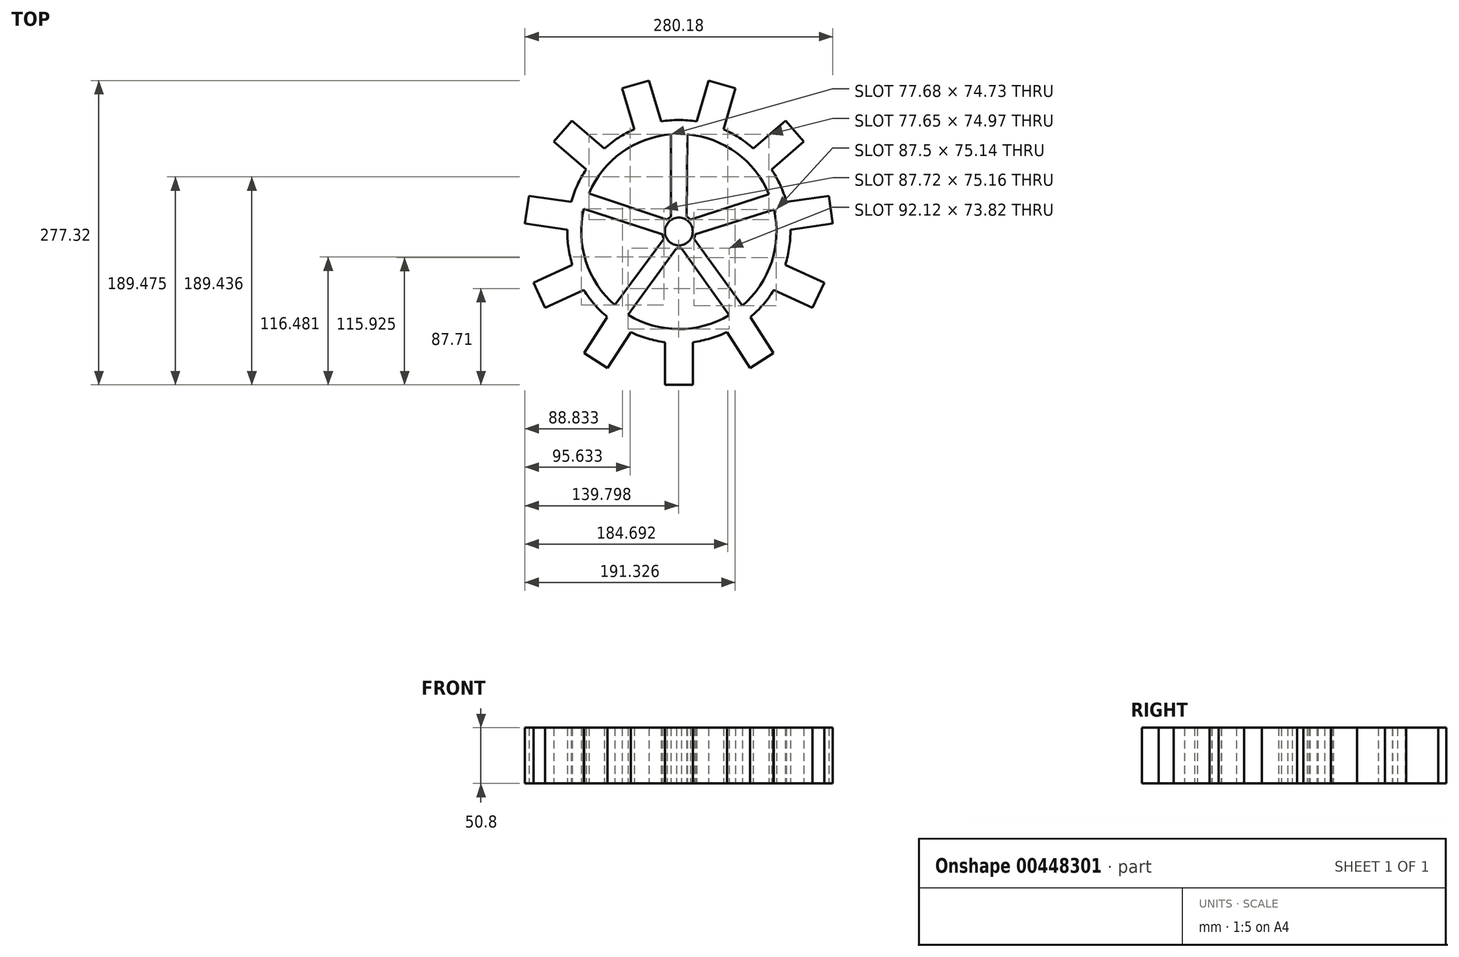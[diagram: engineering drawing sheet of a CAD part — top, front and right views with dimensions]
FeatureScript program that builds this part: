
annotation { "Feature Type Name" : "Feature", "Feature Type Description" : "" }
export const myFeature = defineFeature(function(context is Context, id is Id, definition is map)
    precondition{}
    {
        {
            var Q0;
            Q0=qCreatedBy(makeId("Top.planeOp"),FACE);
            var sketch = newSketch(context, id + "F0", { "sketchPlane" : qUnion([Q0])});
            skCircle(sketch, "E0", {"center": v(0, 0) * mm, "radius": 101.6 * mm});
            skLineSegment(sketch, "E1", {"start": v(-12.7, -100.8) * mm, "end": v(-12.7, -139.7) * mm});
            skLineSegment(sketch, "E2", {"start": v(-12.7, -139.7) * mm, "end": v(12.7, -139.7) * mm});
            skLineSegment(sketch, "E3", {"start": v(12.7, -139.7) * mm, "end": v(12.7, -100.8) * mm});
            skLineSegment(sketch, "E4.1.0", {"start": v(43.81, -91.67) * mm, "end": v(64.84, -124.39) * mm});
            skLineSegment(sketch, "E4.1.1", {"start": v(86.21, -110.66) * mm, "end": v(65.18, -77.93) * mm});
            skLineSegment(sketch, "E4.1.2", {"start": v(64.84, -124.39) * mm, "end": v(86.21, -110.66) * mm});
            skLineSegment(sketch, "E4.2.0", {"start": v(86.42, -53.43) * mm, "end": v(121.8, -69.59) * mm});
            skLineSegment(sketch, "E4.2.1", {"start": v(132.35, -46.48) * mm, "end": v(96.97, -30.32) * mm});
            skLineSegment(sketch, "E4.2.2", {"start": v(121.8, -69.59) * mm, "end": v(132.35, -46.48) * mm});
            skLineSegment(sketch, "E4.3.0", {"start": v(101.58, 1.78) * mm, "end": v(140.09, 7.31) * mm});
            skLineSegment(sketch, "E4.3.1", {"start": v(136.47, 32.45) * mm, "end": v(97.97, 26.92) * mm});
            skLineSegment(sketch, "E4.3.2", {"start": v(140.09, 7.31) * mm, "end": v(136.47, 32.45) * mm});
            skLineSegment(sketch, "E4.4.0", {"start": v(84.5, 56.41) * mm, "end": v(113.9, 81.89) * mm});
            skLineSegment(sketch, "E4.4.1", {"start": v(97.26, 101.08) * mm, "end": v(67.87, 75.61) * mm});
            skLineSegment(sketch, "E4.4.2", {"start": v(113.9, 81.89) * mm, "end": v(97.26, 101.08) * mm});
            skLineSegment(sketch, "E4.5.0", {"start": v(40.59, 93.14) * mm, "end": v(51.54, 130.46) * mm});
            skLineSegment(sketch, "E4.5.1", {"start": v(27.17, 137.62) * mm, "end": v(16.21, 100.3) * mm});
            skLineSegment(sketch, "E4.5.2", {"start": v(51.54, 130.46) * mm, "end": v(27.17, 137.62) * mm});
            skLineSegment(sketch, "E4.6.0", {"start": v(-16.21, 100.3) * mm, "end": v(-27.17, 137.62) * mm});
            skLineSegment(sketch, "E4.6.1", {"start": v(-51.54, 130.46) * mm, "end": v(-40.59, 93.14) * mm});
            skLineSegment(sketch, "E4.6.2", {"start": v(-27.17, 137.62) * mm, "end": v(-51.54, 130.46) * mm});
            skLineSegment(sketch, "E4.7.0", {"start": v(-67.87, 75.61) * mm, "end": v(-97.26, 101.08) * mm});
            skLineSegment(sketch, "E4.7.1", {"start": v(-113.9, 81.89) * mm, "end": v(-84.5, 56.41) * mm});
            skLineSegment(sketch, "E4.7.2", {"start": v(-97.26, 101.08) * mm, "end": v(-113.9, 81.89) * mm});
            skLineSegment(sketch, "E4.8.0", {"start": v(-97.97, 26.92) * mm, "end": v(-136.47, 32.45) * mm});
            skLineSegment(sketch, "E4.8.1", {"start": v(-140.09, 7.31) * mm, "end": v(-101.58, 1.78) * mm});
            skLineSegment(sketch, "E4.8.2", {"start": v(-136.47, 32.45) * mm, "end": v(-140.09, 7.31) * mm});
            skLineSegment(sketch, "E4.9.0", {"start": v(-96.97, -30.32) * mm, "end": v(-132.35, -46.48) * mm});
            skLineSegment(sketch, "E4.9.1", {"start": v(-121.8, -69.59) * mm, "end": v(-86.42, -53.43) * mm});
            skLineSegment(sketch, "E4.9.2", {"start": v(-132.35, -46.48) * mm, "end": v(-121.8, -69.59) * mm});
            skLineSegment(sketch, "E4.10.0", {"start": v(-65.18, -77.93) * mm, "end": v(-86.21, -110.66) * mm});
            skLineSegment(sketch, "E4.10.1", {"start": v(-64.84, -124.39) * mm, "end": v(-43.81, -91.67) * mm});
            skLineSegment(sketch, "E4.10.2", {"start": v(-86.21, -110.66) * mm, "end": v(-64.84, -124.39) * mm});
            skCircle(sketch, "E5", {"center": v(0, 0) * mm, "radius": 12.7 * mm});
            skLineSegment(sketch, "E6", {"start": v(-7.1, 101.35) * mm, "end": v(-7.1, 10.54) * mm});
            skLineSegment(sketch, "E7", {"start": v(7.88, 101.3) * mm, "end": v(7.1, 10.54) * mm});
            skLineSegment(sketch, "E8.1.0", {"start": v(-98.58, 24.58) * mm, "end": v(-12.21, -3.49) * mm});
            skLineSegment(sketch, "E8.1.1", {"start": v(-93.9, 38.8) * mm, "end": v(-7.83, 10) * mm});
            skLineSegment(sketch, "E8.2.0", {"start": v(-53.84, -86.16) * mm, "end": v(-0.46, -12.7) * mm});
            skLineSegment(sketch, "E8.2.1", {"start": v(-65.92, -77.32) * mm, "end": v(-11.93, -4.36) * mm});
            skLineSegment(sketch, "E8.3.0", {"start": v(65.3, -77.83) * mm, "end": v(11.93, -4.36) * mm});
            skLineSegment(sketch, "E8.3.1", {"start": v(53.16, -86.58) * mm, "end": v(0.46, -12.7) * mm});
            skLineSegment(sketch, "E8.4.0", {"start": v(94.2, 38.06) * mm, "end": v(7.83, 10) * mm});
            skLineSegment(sketch, "E8.4.1", {"start": v(98.77, 23.8) * mm, "end": v(12.21, -3.49) * mm});
            skCircle(sketch, "E9", {"center": v(0, 0) * mm, "radius": 88.9 * mm});
            skCircle(sketch, "E10", {"center": v(0, 0) * mm, "radius": 15.24 * mm});
            skSolve(sketch);
        }
        {
            var Q0;
            Q0 = qSketchRegion(id + "F0", true);
            var Q1;
            {var subQ0=sQuery(id+"F0.wireOp",EDGE,"E8.1.0");var subQ1=sQuery(id+"F0.wireOp",EDGE,"E5");var subQ2=makeQuery(id+"F0.imprint","INTERSECT",VERTEX,{"derivedFrom":[subQ1,subQ0]});Q1=makeQuery(id+"F0.imprint","IMPRINT",FACE,{"disambiguationData":[TD([[makeQuery(id+"F0.imprint","IMPRINT",EDGE,{"disambiguationData":[TD([[subQ2,1.0]])],"derivedFrom":subQ1}),-1.0]])]});}
            var Q2;
            {var subQ0=sQuery(id+"F0.wireOp",EDGE,"E6");var subQ1=sQuery(id+"F0.wireOp",EDGE,"E5");var subQ2=makeQuery(id+"F0.imprint","INTERSECT",VERTEX,{"derivedFrom":[subQ1,subQ0]});Q2=makeQuery(id+"F0.imprint","IMPRINT",FACE,{"disambiguationData":[TD([[makeQuery(id+"F0.imprint","IMPRINT",EDGE,{"disambiguationData":[TD([[subQ2,1.0]])],"derivedFrom":subQ1}),-1.0]])]});}
            var Q3;
            {var subQ0=sQuery(id+"F0.wireOp",EDGE,"E8.3.0");var subQ1=sQuery(id+"F0.wireOp",EDGE,"E5");var subQ2=makeQuery(id+"F0.imprint","INTERSECT",VERTEX,{"derivedFrom":[subQ1,subQ0]});Q3=makeQuery(id+"F0.imprint","IMPRINT",FACE,{"disambiguationData":[TD([[makeQuery(id+"F0.imprint","IMPRINT",EDGE,{"disambiguationData":[TD([[subQ2,1.0]])],"derivedFrom":subQ1}),-1.0]])]});}
            var Q4;
            {var subQ0=sQuery(id+"F0.wireOp",EDGE,"E8.2.0");var subQ1=sQuery(id+"F0.wireOp",EDGE,"E5");var subQ2=makeQuery(id+"F0.imprint","INTERSECT",VERTEX,{"derivedFrom":[subQ1,subQ0]});Q4=makeQuery(id+"F0.imprint","IMPRINT",FACE,{"disambiguationData":[TD([[makeQuery(id+"F0.imprint","IMPRINT",EDGE,{"disambiguationData":[TD([[subQ2,1.0]])],"derivedFrom":subQ1}),-1.0]])]});}
            var Q5;
            {var subQ0=sQuery(id+"F0.wireOp",EDGE,"E8.4.0");var subQ1=sQuery(id+"F0.wireOp",EDGE,"E5");var subQ2=makeQuery(id+"F0.imprint","INTERSECT",VERTEX,{"derivedFrom":[subQ1,subQ0]});Q5=makeQuery(id+"F0.imprint","IMPRINT",FACE,{"disambiguationData":[TD([[makeQuery(id+"F0.imprint","IMPRINT",EDGE,{"disambiguationData":[TD([[subQ2,1.0]])],"derivedFrom":subQ1}),-1.0]])]});}
            var Q6;
            {var subQ0=sQuery(id+"F0.wireOp",EDGE,"E9");var subQ1=sQuery(id+"F0.wireOp",EDGE,"E8.2.0");var subQ2=makeQuery(id+"F0.imprint","INTERSECT",VERTEX,{"derivedFrom":[subQ1,subQ0]});Q6=makeQuery(id+"F0.imprint","IMPRINT",FACE,{"disambiguationData":[TD([[makeQuery(id+"F0.imprint","IMPRINT",EDGE,{"disambiguationData":[TD([[subQ2,-1.0]])],"derivedFrom":subQ1}),1.0]])]});}
            var Q7;
            {var subQ0=sQuery(id+"F0.wireOp",EDGE,"E9");var subQ1=sQuery(id+"F0.wireOp",EDGE,"E8.3.0");var subQ2=makeQuery(id+"F0.imprint","INTERSECT",VERTEX,{"derivedFrom":[subQ1,subQ0]});Q7=makeQuery(id+"F0.imprint","IMPRINT",FACE,{"disambiguationData":[TD([[makeQuery(id+"F0.imprint","IMPRINT",EDGE,{"disambiguationData":[TD([[subQ2,-1.0]])],"derivedFrom":subQ1}),1.0]])]});}
            var Q8;
            {var subQ0=sQuery(id+"F0.wireOp",EDGE,"E9");var subQ1=sQuery(id+"F0.wireOp",EDGE,"E8.1.0");var subQ2=makeQuery(id+"F0.imprint","INTERSECT",VERTEX,{"derivedFrom":[subQ1,subQ0]});Q8=makeQuery(id+"F0.imprint","IMPRINT",FACE,{"disambiguationData":[TD([[makeQuery(id+"F0.imprint","IMPRINT",EDGE,{"disambiguationData":[TD([[subQ2,-1.0]])],"derivedFrom":subQ1}),1.0]])]});}
            var Q9;
            {var subQ0=sQuery(id+"F0.wireOp",EDGE,"E8.1.0");var subQ1=sQuery(id+"F0.wireOp",EDGE,"E5");var subQ2=makeQuery(id+"F0.imprint","INTERSECT",VERTEX,{"derivedFrom":[subQ1,subQ0]});Q9=makeQuery(id+"F0.imprint","IMPRINT",FACE,{"disambiguationData":[TD([[makeQuery(id+"F0.imprint","IMPRINT",EDGE,{"disambiguationData":[TD([[subQ2,-1.0]])],"derivedFrom":subQ1}),-1.0]])]});}
            var Q10;
            {var subQ0=sQuery(id+"F0.wireOp",EDGE,"E6");var subQ1=sQuery(id+"F0.wireOp",EDGE,"E5");var subQ2=makeQuery(id+"F0.imprint","INTERSECT",VERTEX,{"derivedFrom":[subQ1,subQ0]});Q10=makeQuery(id+"F0.imprint","IMPRINT",FACE,{"disambiguationData":[TD([[makeQuery(id+"F0.imprint","IMPRINT",EDGE,{"disambiguationData":[TD([[subQ2,-1.0]])],"derivedFrom":subQ1}),-1.0]])]});}
            var Q11;
            {var subQ0=sQuery(id+"F0.wireOp",EDGE,"E7");var subQ1=sQuery(id+"F0.wireOp",EDGE,"E5");var subQ2=makeQuery(id+"F0.imprint","INTERSECT",VERTEX,{"derivedFrom":[subQ1,subQ0]});Q11=makeQuery(id+"F0.imprint","IMPRINT",FACE,{"disambiguationData":[TD([[makeQuery(id+"F0.imprint","IMPRINT",EDGE,{"disambiguationData":[TD([[subQ2,1.0]])],"derivedFrom":subQ1}),-1.0]])]});}
            var Q12;
            {var subQ0=sQuery(id+"F0.wireOp",EDGE,"E9");var subQ1=sQuery(id+"F0.wireOp",EDGE,"E8.4.0");var subQ2=makeQuery(id+"F0.imprint","INTERSECT",VERTEX,{"derivedFrom":[subQ1,subQ0]});Q12=makeQuery(id+"F0.imprint","IMPRINT",FACE,{"disambiguationData":[TD([[makeQuery(id+"F0.imprint","IMPRINT",EDGE,{"disambiguationData":[TD([[subQ2,-1.0]])],"derivedFrom":subQ1}),1.0]])]});}
            var Q13;
            {var subQ0=sQuery(id+"F0.wireOp",EDGE,"E9");var subQ1=sQuery(id+"F0.wireOp",EDGE,"E6");var subQ2=makeQuery(id+"F0.imprint","INTERSECT",VERTEX,{"derivedFrom":[subQ1,subQ0]});Q13=makeQuery(id+"F0.imprint","IMPRINT",FACE,{"disambiguationData":[TD([[makeQuery(id+"F0.imprint","IMPRINT",EDGE,{"disambiguationData":[TD([[subQ2,-1.0]])],"derivedFrom":subQ1}),1.0]])]});}
            var Q14;
            {var subQ0=sQuery(id+"F0.wireOp",EDGE,"E8.2.0");var subQ1=sQuery(id+"F0.wireOp",EDGE,"E5");var subQ2=makeQuery(id+"F0.imprint","INTERSECT",VERTEX,{"derivedFrom":[subQ1,subQ0]});Q14=makeQuery(id+"F0.imprint","IMPRINT",FACE,{"disambiguationData":[TD([[makeQuery(id+"F0.imprint","IMPRINT",EDGE,{"disambiguationData":[TD([[subQ2,-1.0]])],"derivedFrom":subQ1}),-1.0]])]});}
            var Q15;
            {var subQ0=sQuery(id+"F0.wireOp",EDGE,"E8.3.0");var subQ1=sQuery(id+"F0.wireOp",EDGE,"E5");var subQ2=makeQuery(id+"F0.imprint","INTERSECT",VERTEX,{"derivedFrom":[subQ1,subQ0]});Q15=makeQuery(id+"F0.imprint","IMPRINT",FACE,{"disambiguationData":[TD([[makeQuery(id+"F0.imprint","IMPRINT",EDGE,{"disambiguationData":[TD([[subQ2,-1.0]])],"derivedFrom":subQ1}),-1.0]])]});}
            extrude(context, id + "F1", {"entities" : qUnion([Q0, Q1, Q2, Q3, Q4, Q5, Q6, Q7, Q8, Q9, Q10, Q11, Q12, Q13, Q14, Q15]), "depth" : 50.8 * mm});
        }
    });
